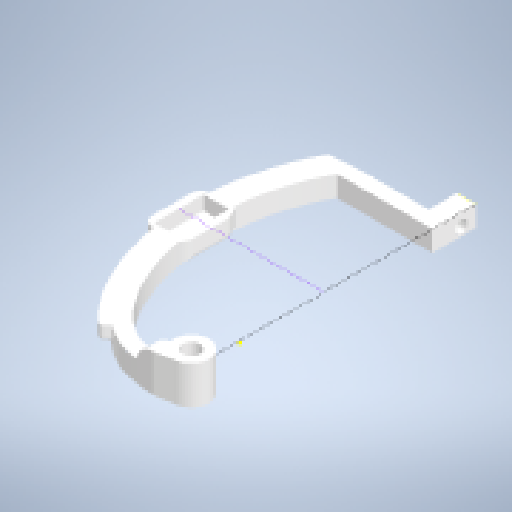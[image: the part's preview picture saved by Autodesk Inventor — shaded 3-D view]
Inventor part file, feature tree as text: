
AUTODESK INVENTOR PART (.ipt)
format: ipt  version: 2025.2 (Build 292293000, 293)  size: 527,872 bytes
history: native  units: in
note: dims shown in document units (in); Inventor stores cm internally (conversion verified against a paired STEP export)
features: sketch x9, fillet x6, extrude x5
ambient origin geometry x8: Origin, YZ Plane, XZ Plane, XY Plane, X Axis, Y Axis, Z Axis, Center Point
bodies: Solid1 (feature_tree), Body1 (feature_tree)
feature tree (20):
  sketch  "Sketch1"  dims[d5=0.1693in d6=0.2441in]
  sketch  "Sketch2"  dims[d7=0.0787in d8=0.0in d9=0.1063in d10=0.2047in d11=0.0591in d12=0.0in d13=0.0787in d14=0.0394in d15=0.0394in d16=0.0197in]
  sketch  "Sketch4"  dims[d17=0.0197in d18=0.0787in]
  sketch  "Sketch5"  dims[d19=0.7992in d20=0.0in d21=0.1742in d22=0.0in]
  extrude  "Extrusion1"  Depth=0.2441in
  extrude  "Extrusion2"  Depth=0.1063in
  fillet  "Fillet1"  Radius=0.2047in
  fillet  "Fillet2"  Radius=0.0591in
  fillet  "Fillet3"  Radius=0.0787in
  fillet  "Fillet4"  Radius=0.0394in
  fillet  "Fillet5"  Radius=0.0394in
  fillet  "Fillet6"  Radius=0.0197in
  extrude  "Extrusion3"  Depth=0.0787in
  extrude  "Extrusion4"  Depth=0.1742in TaperAngle=0.0deg
  extrude  "Extrusion5"  [1 undecoded]
  sketch  "Sketch6"  dims[d23=0.1742in d24=0.0in]
  sketch  "Sketch7"
  sketch  "Sketch8"
  sketch  "Sketch9"
  sketch  "Sketch10"
note: 1 required parameter value undecoded (feature->parameter linkage not recoverable at this tier; creation-order binding heuristic only, values carry confidence <= 0.55)
